# Revit family: SOL31
name_source: partatom
category: Plumbing Fixtures
revit_build: Autodesk Revit 2015 (Build: 20140606_1530(x64)
units: mm (PartAtom-declared; Revit-internal decimal feet)

## types (5) — shared parameters
Aluminum = Aluminum
Chrome = Chrome - Polished
Glass = Glass
Manufacturer = SanSwiss
Model = SOL31
Seal = Seal
Type Comments = SOLINO
URL = www.sanswiss.com

## per-type parameters (varying)
| type | A | B | C | holder type |
| 1000 | 1000 mm  [stored 3.28084 ft] | 330 mm | 670 mm | holder : A=1000 |
| 1400 | 1400 mm | 530 mm  [stored 1.73885 ft] | 870 mm | holder : A=1400 |
| 900 | 900 mm | 230 mm  [stored 0.754593 ft] | 670 mm | holder : A=900 |
| 1200 | 1200 mm | 430 mm | 770 mm | holder : A=1200 |
| 1100 | 1100 mm | 430 mm | 670 mm | holder : A=1200 |

note: [stored X ft] marks values corroborated as IEEE doubles in the binary element streams (Revit-internal decimal feet)

## geometry (parser evidence)
native form markers: Sweep x9
no freeform markers — native parametric forms only
